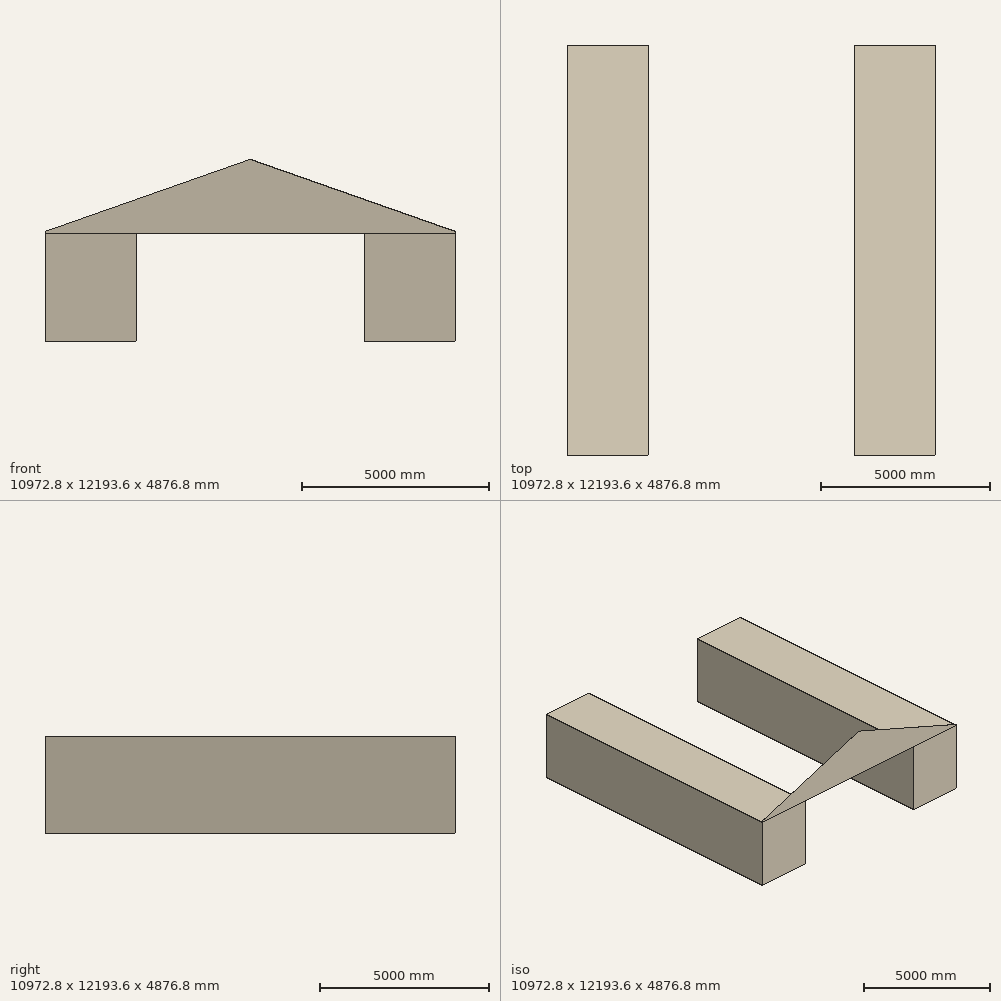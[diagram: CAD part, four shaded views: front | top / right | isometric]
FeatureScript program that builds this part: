
annotation { "Feature Type Name" : "Feature", "Feature Type Description" : "" }
export const myFeature = defineFeature(function(context is Context, id is Id, definition is map)
    precondition{}
    {
        {
            var Q0;
            Q0=qCreatedBy(makeId("Front.planeOp"),FACE);
            var sketch = newSketch(context, id + "F0", { "sketchPlane" : qUnion([Q0])});
            skLineSegment(sketch, "E0", {"start": v(0, 0) * mm, "end": v(0, 50.8) * mm});
            skLineSegment(sketch, "E1", {"start": v(0, 50.8) * mm, "end": v(5486.4, 1981.2) * mm});
            skLineSegment(sketch, "E2", {"start": v(5486.4, 1981.2) * mm, "end": v(10972.8, 50.8) * mm});
            skLineSegment(sketch, "E3", {"start": v(0, 0) * mm, "end": v(10972.8, 0) * mm});
            skLineSegment(sketch, "E4", {"start": v(10972.8, 0) * mm, "end": v(10972.8, 50.8) * mm});
            skSolve(sketch);
        }
        {
            var Q0;
            Q0 = qSketchRegion(id + "F0", true);
            extrude(context, id + "F1", {"entities" : qUnion([Q0]), "depth" : 1.6 * mm});
        }
        {
            var Q0;
            Q0=qCreatedBy(makeId("Front.planeOp"),FACE);
            var sketch = newSketch(context, id + "F2", { "sketchPlane" : qUnion([Q0])});
            skLineSegment(sketch, "E5.bottom", {"start": v(0, 0) * mm, "end": v(2425.7, 0) * mm});
            skLineSegment(sketch, "E5.top", {"start": v(0, -2895.6) * mm, "end": v(2425.7, -2895.6) * mm});
            skLineSegment(sketch, "E5.left", {"start": v(0, 0) * mm, "end": v(0, -2895.6) * mm});
            skLineSegment(sketch, "E5.right", {"start": v(2425.7, 0) * mm, "end": v(2425.7, -2895.6) * mm});
            skLineSegment(sketch, "E6.bottom", {"start": v(10972.8, 0) * mm, "end": v(8547.1, 0) * mm});
            skLineSegment(sketch, "E6.top", {"start": v(10972.8, -2895.6) * mm, "end": v(8547.1, -2895.6) * mm});
            skLineSegment(sketch, "E6.left", {"start": v(10972.8, 0) * mm, "end": v(10972.8, -2895.6) * mm});
            skLineSegment(sketch, "E6.right", {"start": v(8547.1, 0) * mm, "end": v(8547.1, -2895.6) * mm});
            skSolve(sketch);
        }
        {
            var Q0;
            Q0=makeQuery(id+"F2.imprint","IMPRINT",FACE,{"disambiguationData":[TD([[makeQuery(id+"F2.imprint","IMPRINT",EDGE,{"derivedFrom":sQuery(id+"F2.wireOp",EDGE,"E5.bottom")}),-1.0]])]});
            var Q1;
            Q1=makeQuery(id+"F2.imprint","IMPRINT",FACE,{"disambiguationData":[TD([[makeQuery(id+"F2.imprint","IMPRINT",EDGE,{"derivedFrom":sQuery(id+"F2.wireOp",EDGE,"E6.bottom")}),1.0]])]});
            extrude(context, id + "F3", {"entities" : qUnion([Q0, Q1]), "operationType" : NewBodyOperationType.ADD, "oppositeDirection" : true, "depth" : 12192 * mm});
        }
    });
